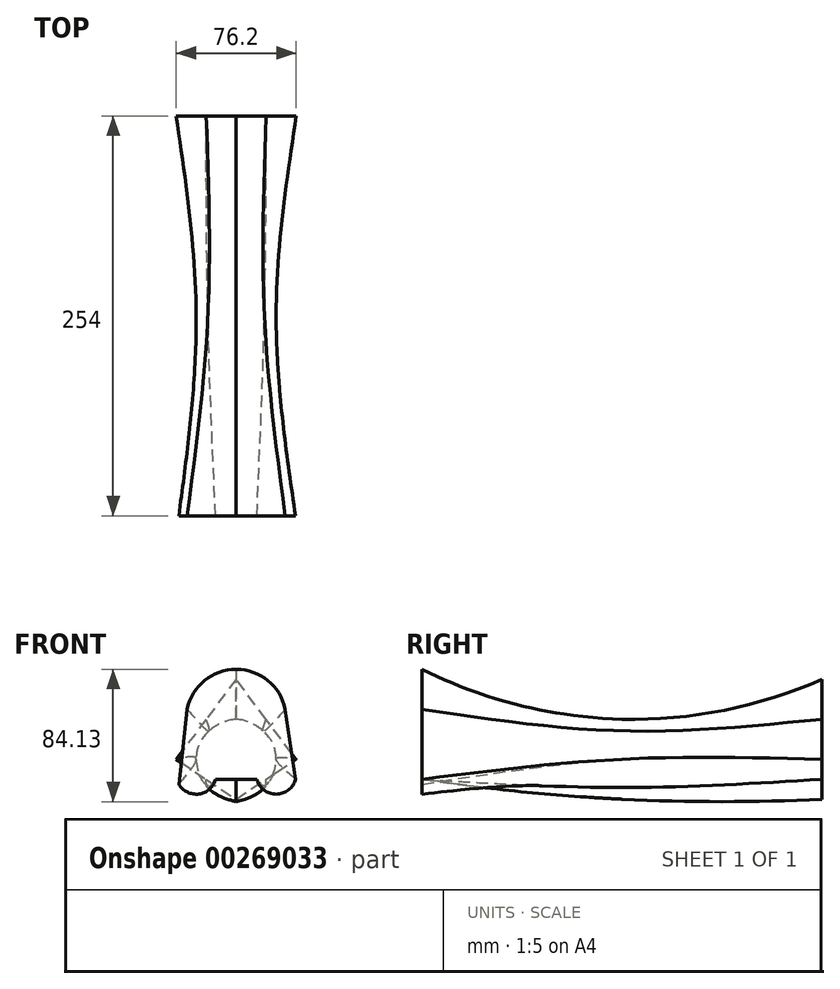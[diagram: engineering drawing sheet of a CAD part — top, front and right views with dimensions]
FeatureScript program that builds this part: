
annotation { "Feature Type Name" : "Feature", "Feature Type Description" : "" }
export const myFeature = defineFeature(function(context is Context, id is Id, definition is map)
    precondition{}
    {
        {
            var Q0;
            Q0=qCreatedBy(makeId("Front.planeOp"),FACE);
            cPlane(context, id + "F0", {"entities" : qUnion([Q0]), "cplaneType" : CPlaneType.OFFSET, "offset" : 127 * mm, "width" : 152.4 * mm, "height" : 152.4 * mm});
        }
        {
            var Q0;
            Q0=qCreatedBy(makeId("Front.planeOp"),FACE);
            cPlane(context, id + "F1", {"entities" : qUnion([Q0]), "cplaneType" : CPlaneType.OFFSET, "offset" : 254 * mm, "width" : 152.4 * mm, "height" : 152.4 * mm});
        }
        {
            var Q0;
            Q0=qCreatedBy(id+"F1.planeOp",FACE);
            var sketch = newSketch(context, id + "F2", { "sketchPlane" : qUnion([Q0])});
            skArc(sketch, "E0", {"start": v(-36.4, -15.88) * mm, "mid": v(-23.68, -22.1) * mm, "end": v(-13.1, -12.7) * mm});
            skArc(sketch, "E1", {"start": v(13.1, -12.7) * mm, "mid": v(25.4, -22.23) * mm, "end": v(37.7, -12.7) * mm});
            skLineSegment(sketch, "E2", {"start": v(-13.1, -12.7) * mm, "end": v(13.1, -12.7) * mm});
            skArc(sketch, "E3", {"start": v(-31.1, 31.75) * mm, "mid": v(0, 57.15) * mm, "end": v(31.1, 31.75) * mm});
            skLineSegment(sketch, "E4", {"start": v(-31.1, 31.75) * mm, "end": v(-36.4, -15.88) * mm});
            skLineSegment(sketch, "E5", {"start": v(31.1, 31.75) * mm, "end": v(37.7, -12.7) * mm});
            skSolve(sketch);
        }
        {
            var Q0;
            Q0=qCreatedBy(id+"F0.planeOp",FACE);
            var sketch = newSketch(context, id + "F3", { "sketchPlane" : qUnion([Q0])});
            skCircle(sketch, "E6", {"center": v(0, 0) * mm, "radius": 25.4 * mm});
            skPoint(sketch, "E7", {"position": v(-25.4, 0) * mm});
            skPoint(sketch, "E8", {"position": v(25.4, 0) * mm});
            skSolve(sketch);
        }
        {
            var Q0;
            Q0=qCreatedBy(makeId("Front.planeOp"),FACE);
            var sketch = newSketch(context, id + "F4", { "sketchPlane" : qUnion([Q0])});
            skLineSegment(sketch, "E9", {"start": v(0, 50.8) * mm, "end": v(-38.1, 0) * mm});
            skLineSegment(sketch, "E10", {"start": v(-38.1, 0) * mm, "end": v(0, -25.4) * mm});
            skLineSegment(sketch, "E11", {"start": v(0, -25.4) * mm, "end": v(38.1, 0) * mm});
            skLineSegment(sketch, "E12", {"start": v(38.1, 0) * mm, "end": v(0, 50.8) * mm});
            skSolve(sketch);
        }
        {
            var Q0;
            Q0=qCreatedBy(makeId("Right.planeOp"),FACE);
            var sketch = newSketch(context, id + "F5", { "sketchPlane" : qUnion([Q0])});
            skArc(sketch, "E13", {"start": v(-254, 57.15) * mm, "mid": v(-127.71, 25.42) * mm, "end": v(0, 50.8) * mm});
            skArc(sketch, "E14", {"start": v(-254, -12.7) * mm, "mid": v(-127.32, -25.38) * mm, "end": v(0, -25.4) * mm});
            skSolve(sketch);
        }
        {
            var Q0;
            Q0=makeQuery(id+"F2.imprint","IMPRINT",FACE,{"disambiguationData":[TD([[makeQuery(id+"F2.imprint","IMPRINT",EDGE,{"derivedFrom":sQuery(id+"F2.wireOp",EDGE,"E0")}),1.0]])]});
            var Q1;
            Q1=makeQuery(id+"F3.imprint","IMPRINT",FACE,{"disambiguationData":[TD([[makeQuery(id+"F3.imprint","IMPRINT",EDGE,{"derivedFrom":sQuery(id+"F3.wireOp",EDGE,"E6")}),1.0]])]});
            var Q2;
            Q2=makeQuery(id+"F4.imprint","IMPRINT",FACE,{"disambiguationData":[TD([[makeQuery(id+"F4.imprint","IMPRINT",EDGE,{"derivedFrom":sQuery(id+"F4.wireOp",EDGE,"E9")}),1.0]])]});
            var Q3;
            Q3=sQuery(id+"F5.wireOp",EDGE,"E13");
            var Q4;
            Q4=sQuery(id+"F5.wireOp",EDGE,"E14");
            var Q5;
            Q5=sQuery(id+"F4.wireOp",VERTEX,"E10.start");
            var Q6;
            Q6=sQuery(id+"F3.wireOp",VERTEX,"E7");
            var Q7;
            Q7=sQuery(id+"F2.wireOp",VERTEX,"E4.end");
            loft(context, id + "F6", {"addGuides" : true, "sheetProfilesArray" : [{ "sheetProfileEntities" : qUnion([Q0]) }, { "sheetProfileEntities" : qUnion([Q1]) }, { "sheetProfileEntities" : qUnion([Q2]) }], "guidesArray" : [{ "guideEntities" : qUnion([Q3]), "guideDerivativeType" : LoftGuideDerivativeType.DEFAULT, "guideDerivativeMagnitude" : 1 }, { "guideEntities" : qUnion([Q4]), "guideDerivativeType" : LoftGuideDerivativeType.DEFAULT, "guideDerivativeMagnitude" : 1 }], "matchConnections" : true, "connections" : [{ "connectionEntities" : qUnion([Q5, Q6, Q7]), "connectionEdgeQueries" : qUnion([]), "connectionEdgeParameters" : [] }]});
        }
    });
